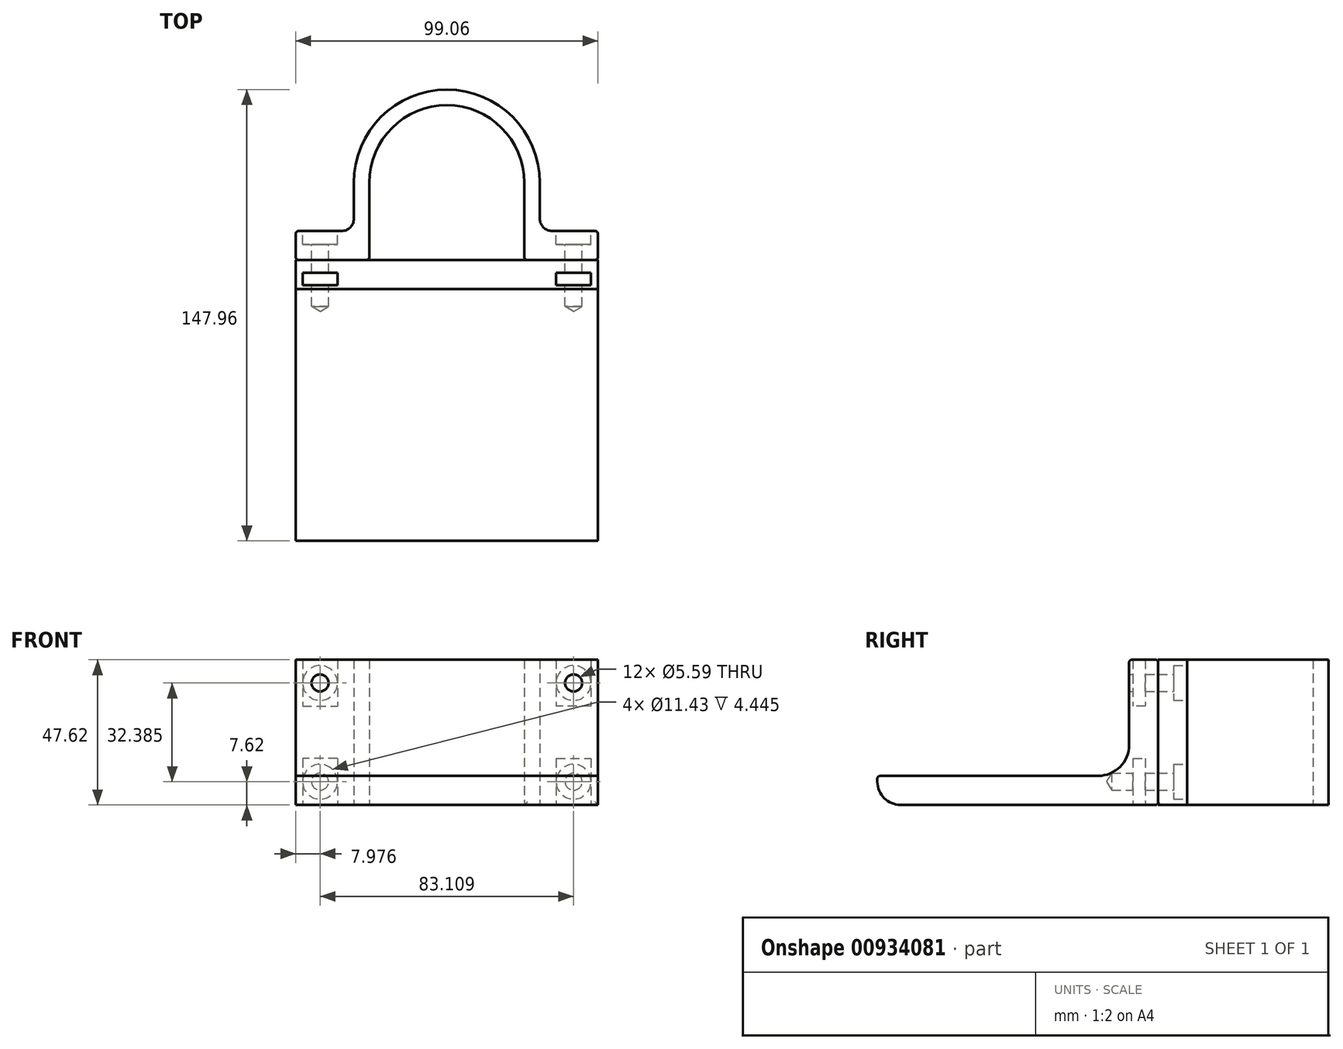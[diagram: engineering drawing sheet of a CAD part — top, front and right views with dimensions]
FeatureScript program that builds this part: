
annotation { "Feature Type Name" : "Feature", "Feature Type Description" : "" }
export const myFeature = defineFeature(function(context is Context, id is Id, definition is map)
    precondition{}
    {
        {
            var Q0;
            Q0=qCreatedBy(makeId("Top.planeOp"),FACE);
            var sketch = newSketch(context, id + "F0", { "sketchPlane" : qUnion([Q0])});
            skCircle(sketch, "E0", {"center": v(0, 0) * mm, "radius": 25.4 * mm, "construction": true});
            skLineSegment(sketch, "E1", {"start": v(-53.77, -25.4) * mm, "end": v(62.38, -25.4) * mm, "construction": true});
            skLineSegment(sketch, "E2", {"start": v(-25.4, 0) * mm, "end": v(-25.4, -25.4) * mm});
            skLineSegment(sketch, "E3", {"start": v(-25.4, -25.4) * mm, "end": v(-49.53, -25.4) * mm});
            skLineSegment(sketch, "E4", {"start": v(-49.53, -25.4) * mm, "end": v(-49.53, -15.88) * mm});
            skLineSegment(sketch, "E5", {"start": v(-49.53, -15.88) * mm, "end": v(-30.48, -15.88) * mm});
            skLineSegment(sketch, "E6", {"start": v(-30.48, -15.88) * mm, "end": v(-30.48, 0) * mm});
            skArc(sketch, "E7", {"start": v(-25.4, 0) * mm, "mid": v(-17.96, 17.96) * mm, "end": v(0, 25.4) * mm});
            skArc(sketch, "E8", {"start": v(-30.48, 0) * mm, "mid": v(-21.55, 21.55) * mm, "end": v(0, 30.48) * mm});
            skLineSegment(sketch, "E9", {"start": v(0, 30.48) * mm, "end": v(0, 25.4) * mm});
            skArc(sketch, "E10.MirrorCS", {"start": v(30.48, 0) * mm, "mid": v(21.55, 21.55) * mm, "end": v(0, 30.48) * mm});
            skLineSegment(sketch, "E11.MirrorCS", {"start": v(30.48, -15.88) * mm, "end": v(30.48, 0) * mm});
            skLineSegment(sketch, "E12.MirrorCS", {"start": v(25.4, 0) * mm, "end": v(25.4, -25.4) * mm});
            skLineSegment(sketch, "E13.MirrorCS", {"start": v(49.53, -25.4) * mm, "end": v(49.53, -15.88) * mm});
            skLineSegment(sketch, "E14.MirrorCS", {"start": v(49.53, -15.88) * mm, "end": v(30.48, -15.88) * mm});
            skArc(sketch, "E15.MirrorCS", {"start": v(25.4, 0) * mm, "mid": v(17.96, 17.96) * mm, "end": v(0, 25.4) * mm});
            skLineSegment(sketch, "E16.MirrorCS", {"start": v(25.4, -25.4) * mm, "end": v(49.53, -25.4) * mm});
            skSolve(sketch);
        }
        {
            var Q0;
            Q0 = qSketchRegion(id + "F0", true);
            extrude(context, id + "F1", {"entities" : qUnion([Q0]), "depth" : 38.1 * mm + 9.52 * mm, "offsetDistance" : 25.4 * mm});
        }
        {
            var Q0;
            Q0=makeQuery(id+"F1.opExtrude","SWEPT_EDGE",EDGE,{"disambiguationData":[OSD([sQuery(id+"F0.wireOp",EDGE,"E5"),sQuery(id+"F0.wireOp",EDGE,"E6")])]});
            var Q1;
            Q1=makeQuery(id+"F1.opExtrude","SWEPT_EDGE",EDGE,{"disambiguationData":[OSD([sQuery(id+"F0.wireOp",EDGE,"E11.MirrorCS"),sQuery(id+"F0.wireOp",EDGE,"E14.MirrorCS")])]});
            fillet(context, id + "F2", {"entities" : qUnion([Q0, Q1]), "radius" : 4.06 * mm, "tangentPropagation" : true, "allowEdgeOverflow" : false});
        }
        {
            var Q0;
            Q0=makeQuery(id+"F1.opExtrude","SWEPT_EDGE",EDGE,{"disambiguationData":[OSD([sQuery(id+"F0.wireOp",EDGE,"E13.MirrorCS"),sQuery(id+"F0.wireOp",EDGE,"E14.MirrorCS")])]});
            var Q1;
            Q1=makeQuery(id+"F1.opExtrude","SWEPT_EDGE",EDGE,{"disambiguationData":[OSD([sQuery(id+"F0.wireOp",EDGE,"E13.MirrorCS"),sQuery(id+"F0.wireOp",EDGE,"E16.MirrorCS")])]});
            var Q2;
            Q2=makeQuery(id+"F1.opExtrude","SWEPT_EDGE",EDGE,{"disambiguationData":[OSD([sQuery(id+"F0.wireOp",EDGE,"E12.MirrorCS"),sQuery(id+"F0.wireOp",EDGE,"E16.MirrorCS")])]});
            var Q3;
            Q3=makeQuery(id+"F1.opExtrude","CAP_EDGE",EDGE,{"disambiguationData":[OSD([sQuery(id+"F0.wireOp",EDGE,"E16.MirrorCS")])],"isStart":true});
            var Q4;
            Q4=makeQuery(id+"F1.opExtrude","SWEPT_EDGE",EDGE,{"disambiguationData":[OSD([sQuery(id+"F0.wireOp",EDGE,"E2"),sQuery(id+"F0.wireOp",EDGE,"E3")])]});
            var Q5;
            Q5=makeQuery(id+"F1.opExtrude","SWEPT_EDGE",EDGE,{"disambiguationData":[OSD([sQuery(id+"F0.wireOp",EDGE,"E3"),sQuery(id+"F0.wireOp",EDGE,"E4")])]});
            var Q6;
            Q6=makeQuery(id+"F1.opExtrude","SWEPT_EDGE",EDGE,{"disambiguationData":[OSD([sQuery(id+"F0.wireOp",EDGE,"E4"),sQuery(id+"F0.wireOp",EDGE,"E5")])]});
            fillet(context, id + "F3", {"entities" : qUnion([Q0, Q1, Q2, Q3, Q4, Q5, Q6]), "radius" : 0.97 * mm, "tangentPropagation" : true, "allowEdgeOverflow" : false});
        }
        {
            var Q0;
            Q0=makeQuery(id+"F1.opExtrude","SWEPT_FACE",FACE,{"disambiguationData":[OSD([sQuery(id+"F0.wireOp",EDGE,"E5")])]});
            var sketch = newSketch(context, id + "F4", { "sketchPlane" : qUnion([Q0])});
            skLineSegment(sketch, "E17", {"start": v(-48.56, 47.62) * mm, "end": v(-34.54, 47.62) * mm, "construction": true});
            skLineSegment(sketch, "E18", {"start": v(-41.55, 47.62) * mm, "end": v(-41.55, 23.81) * mm, "construction": true});
            skLineSegment(sketch, "E19", {"start": v(-41.55, 23.81) * mm, "end": v(-41.55, 0) * mm, "construction": true});
            skPoint(sketch, "E20", {"position": v(-41.55, 40) * mm});
            skPoint(sketch, "E21", {"position": v(-41.55, 7.62) * mm});
            skPoint(sketch, "E22.MirrorP", {"position": v(41.55, 40) * mm});
            skPoint(sketch, "E23.MirrorP", {"position": v(41.55, 7.62) * mm});
            skSolve(sketch);
        }
        {
            var Q0;
            Q0=sQuery(id+"F4.wireOp",VERTEX,"E20");
            var Q1;
            Q1=sQuery(id+"F4.wireOp",VERTEX,"E21");
            var Q2;
            Q2=sQuery(id+"F4.wireOp",VERTEX,"E22.MirrorP");
            var Q3;
            Q3=sQuery(id+"F4.wireOp",VERTEX,"E23.MirrorP");
            var Q4;
            Q4=makeQuery(id+"F1.opExtrude","SWEPT_BODY",BODY,{"disambiguationData":[OSD([sQuery(id+"F0.wireOp",EDGE,"E2"),sQuery(id+"F0.wireOp",EDGE,"E3"),sQuery(id+"F0.wireOp",EDGE,"E4"),sQuery(id+"F0.wireOp",EDGE,"E5"),sQuery(id+"F0.wireOp",EDGE,"E6"),sQuery(id+"F0.wireOp",EDGE,"E7"),sQuery(id+"F0.wireOp",EDGE,"E8"),sQuery(id+"F0.wireOp",EDGE,"E10.MirrorCS"),sQuery(id+"F0.wireOp",EDGE,"E11.MirrorCS"),sQuery(id+"F0.wireOp",EDGE,"E12.MirrorCS"),sQuery(id+"F0.wireOp",EDGE,"E13.MirrorCS"),sQuery(id+"F0.wireOp",EDGE,"E14.MirrorCS"),sQuery(id+"F0.wireOp",EDGE,"E15.MirrorCS"),sQuery(id+"F0.wireOp",EDGE,"E16.MirrorCS")])]});
            hole(context, id + "F5", {"style" : HoleStyle.C_BORE, "endStyle" : HoleEndStyle.THROUGH, "holeDiameter" : 5.6 * mm, "cBoreDiameter" : 11.43 * mm, "cBoreDepth" : 4.44 * mm, "majorDiameter" : 6.35 * mm, "isTappedThrough" : true, "tappedDepth" : 12.7 * mm, "tapClearance" : 3, "locations" : qUnion([Q0, Q1, Q2, Q3]), "scope" : qUnion([Q4])});
        }
        {
            var Q0;
            Q0=qCreatedBy(makeId("Right.planeOp"),FACE);
            var sketch = newSketch(context, id + "F6", { "sketchPlane" : qUnion([Q0])});
            skLineSegment(sketch, "E24", {"start": v(-34.93, 47.62) * mm, "end": v(-34.93, 9.52) * mm});
            skLineSegment(sketch, "E25", {"start": v(-34.93, 9.52) * mm, "end": v(-117.48, 9.52) * mm});
            skLineSegment(sketch, "E26", {"start": v(-117.48, 9.52) * mm, "end": v(-117.48, 0) * mm});
            skLineSegment(sketch, "E27", {"start": v(-117.48, 0) * mm, "end": v(-25.4, 0) * mm});
            skLineSegment(sketch, "E28", {"start": v(-25.4, 0) * mm, "end": v(-25.4, 47.62) * mm});
            skLineSegment(sketch, "E29", {"start": v(-25.4, 47.62) * mm, "end": v(-34.93, 47.62) * mm});
            skLineSegment(sketch, "E30.bottom", {"start": v(-123.83, 50.16) * mm, "end": v(-47.63, 50.16) * mm, "construction": true});
            skLineSegment(sketch, "E30.top", {"start": v(-123.83, 12.06) * mm, "end": v(-47.63, 12.06) * mm, "construction": true});
            skLineSegment(sketch, "E30.left", {"start": v(-123.83, 50.16) * mm, "end": v(-123.83, 12.06) * mm, "construction": true});
            skLineSegment(sketch, "E30.right", {"start": v(-47.63, 50.16) * mm, "end": v(-47.63, 12.06) * mm, "construction": true});
            skLineSegment(sketch, "E31", {"start": v(-25.4, 68.97) * mm, "end": v(-25.4, -59.18) * mm, "construction": true});
            skSolve(sketch);
        }
        {
            var Q0;
            Q0 = qSketchRegion(id + "F6", true);
            extrude(context, id + "F7", {"entities" : qUnion([Q0]), "endBound" : BoundingType.SYMMETRIC, "depth" : 99.06 * mm, "offsetDistance" : 25.4 * mm});
        }
        {
            var Q0;
            Q0=makeQuery(id+"F7.opExtrude","SWEPT_EDGE",EDGE,{"disambiguationData":[OSD([sQuery(id+"F6.wireOp",EDGE,"E24"),sQuery(id+"F6.wireOp",EDGE,"E25")])]});
            fillet(context, id + "F8", {"entities" : qUnion([Q0]), "radius" : 10.16 * mm, "tangentPropagation" : true, "allowEdgeOverflow" : false});
        }
        {
            var Q0;
            Q0=makeQuery(id+"F7.opExtrude","SWEPT_EDGE",EDGE,{"disambiguationData":[OSD([sQuery(id+"F6.wireOp",EDGE,"E26"),sQuery(id+"F6.wireOp",EDGE,"E27")])]});
            fillet(context, id + "F9", {"entities" : qUnion([Q0]), "radius" : 7.62 * mm, "tangentPropagation" : true, "allowEdgeOverflow" : false});
        }
        {
            var Q0;
            Q0=makeQuery(id+"F7.opExtrude","SWEPT_EDGE",EDGE,{"disambiguationData":[OSD([sQuery(id+"F6.wireOp",EDGE,"E25"),sQuery(id+"F6.wireOp",EDGE,"E26")])]});
            var Q1;
            Q1=makeQuery(id+"F7.opExtrude","SWEPT_EDGE",EDGE,{"disambiguationData":[OSD([sQuery(id+"F6.wireOp",EDGE,"E24"),sQuery(id+"F6.wireOp",EDGE,"E29")])]});
            var Q2;
            Q2=makeQuery(id+"F7.opExtrude","SWEPT_EDGE",EDGE,{"disambiguationData":[OSD([sQuery(id+"F6.wireOp",EDGE,"E28"),sQuery(id+"F6.wireOp",EDGE,"E29")])]});
            var Q3;
            Q3=makeQuery(id+"F7.opExtrude","SWEPT_EDGE",EDGE,{"disambiguationData":[OSD([sQuery(id+"F6.wireOp",EDGE,"E27"),sQuery(id+"F6.wireOp",EDGE,"E28")])]});
            fillet(context, id + "F10", {"entities" : qUnion([Q0, Q1, Q2, Q3]), "radius" : 0.95 * mm, "tangentPropagation" : true, "allowEdgeOverflow" : false});
        }
        {
            var Q0;
            Q0=qCreatedBy(makeId("Top.planeOp"),FACE);
            var sketch = newSketch(context, id + "F11", { "sketchPlane" : qUnion([Q0])});
            skLineSegment(sketch, "E32.bottom", {"start": v(35.84, -33.66) * mm, "end": v(47.27, -33.65) * mm});
            skLineSegment(sketch, "E32.top", {"start": v(35.84, -29.6) * mm, "end": v(47.27, -29.6) * mm});
            skLineSegment(sketch, "E32.left", {"start": v(35.84, -33.65) * mm, "end": v(35.84, -29.6) * mm});
            skLineSegment(sketch, "E32.right", {"start": v(47.27, -33.65) * mm, "end": v(47.27, -29.6) * mm});
            skLineSegment(sketch, "E33.MirrorCS", {"start": v(-47.27, -33.65) * mm, "end": v(-47.27, -29.6) * mm});
            skLineSegment(sketch, "E34.MirrorCS", {"start": v(-35.84, -29.6) * mm, "end": v(-47.27, -29.6) * mm});
            skLineSegment(sketch, "E35.MirrorCS", {"start": v(-35.84, -33.65) * mm, "end": v(-35.84, -29.6) * mm});
            skLineSegment(sketch, "E36.MirrorCS", {"start": v(-35.84, -33.66) * mm, "end": v(-47.27, -33.65) * mm});
            skLineSegment(sketch, "E37", {"start": v(41.55, 45.5) * mm, "end": v(41.55, -65.12) * mm, "construction": true});
            skPoint(sketch, "E38", {"position": v(41.55, -33.65) * mm});
            skLineSegment(sketch, "E39", {"start": v(16.09, -34.93) * mm, "end": v(61.76, -34.92) * mm, "construction": true});
            skSolve(sketch);
        }
        {
            var Q0;
            Q0 = qSketchRegion(id + "F11", true);
            extrude(context, id + "F12", {"entities" : qUnion([Q0]), "operationType" : NewBodyOperationType.REMOVE, "depth" : 15.24 * mm, "offsetDistance" : 25.4 * mm});
        }
        {
            var Q0;
            Q0=sQuery(id+"F4.wireOp",VERTEX,"E21");
            var Q1;
            Q1=sQuery(id+"F4.wireOp",VERTEX,"E23.MirrorP");
            var Q2;
            Q2=makeQuery(id+"F7.opExtrude","SWEPT_BODY",BODY,{"disambiguationData":[OSD([sQuery(id+"F6.wireOp",EDGE,"E24"),sQuery(id+"F6.wireOp",EDGE,"E25"),sQuery(id+"F6.wireOp",EDGE,"E26"),sQuery(id+"F6.wireOp",EDGE,"E27"),sQuery(id+"F6.wireOp",EDGE,"E28"),sQuery(id+"F6.wireOp",EDGE,"E29")])]});
            hole(context, id + "F13", {"style" : HoleStyle.SIMPLE, "endStyle" : HoleEndStyle.BLIND, "holeDiameter" : 5.6 * mm, "majorDiameter" : 6.35 * mm, "holeDepth" : 15.24 * mm, "isTappedThrough" : true, "tappedDepth" : 12.7 * mm, "tapClearance" : 3, "locations" : qUnion([Q0, Q1]), "scope" : qUnion([Q2])});
        }
        {
            var Q0;
            Q0=sQuery(id+"F4.wireOp",VERTEX,"E20");
            var Q1;
            Q1=sQuery(id+"F4.wireOp",VERTEX,"E22.MirrorP");
            var Q2;
            Q2=makeQuery(id+"F7.opExtrude","SWEPT_BODY",BODY,{"disambiguationData":[OSD([sQuery(id+"F6.wireOp",EDGE,"E24"),sQuery(id+"F6.wireOp",EDGE,"E25"),sQuery(id+"F6.wireOp",EDGE,"E26"),sQuery(id+"F6.wireOp",EDGE,"E27"),sQuery(id+"F6.wireOp",EDGE,"E28"),sQuery(id+"F6.wireOp",EDGE,"E29")])]});
            hole(context, id + "F14", {"style" : HoleStyle.SIMPLE, "endStyle" : HoleEndStyle.THROUGH, "holeDiameter" : 5.6 * mm, "majorDiameter" : 6.35 * mm, "isTappedThrough" : true, "tappedDepth" : 12.7 * mm, "tapClearance" : 3, "locations" : qUnion([Q0, Q1]), "scope" : qUnion([Q2])});
        }
        {
            var Q0;
            Q0 = qSketchRegion(id + "F11", true);
            var Q1;
            Q1=makeQuery(id+"F7.opExtrude","SWEPT_FACE",FACE,{"disambiguationData":[OSD([sQuery(id+"F6.wireOp",EDGE,"E29")])]});
            var Q2;
            Q2=makeQuery(id+"F7.opExtrude","SWEPT_FACE",FACE,{"disambiguationData":[OSD([sQuery(id+"F6.wireOp",EDGE,"E29")])]});
            extrude(context, id + "F15", {"entities" : qUnion([Q0]), "operationType" : NewBodyOperationType.REMOVE, "endBound" : BoundingType.UP_TO_SURFACE, "depth" : 25.4 * mm, "endBoundEntityFace" : qUnion([Q1]), "offsetDistance" : 25.4 * mm, "hasSecondDirection" : true, "secondDirectionBound" : SecondDirectionBoundingType.UP_TO_SURFACE, "secondDirectionOppositeDirection" : false, "secondDirectionDepth" : 25.4 * mm, "secondDirectionBoundEntityFace" : qUnion([Q2]), "hasSecondDirectionOffset" : true, "secondDirectionOffsetDistance" : 15.24 * mm});
        }
    });
